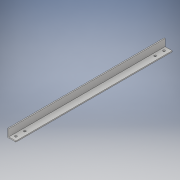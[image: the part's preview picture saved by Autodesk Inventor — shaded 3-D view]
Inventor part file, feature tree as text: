
AUTODESK INVENTOR PART (.ipt)
format: ipt  version: 2017 (Build 210142000, 142)  size: 126,976 bytes
history: native  units: in
note: dims shown in document units (in); Inventor stores cm internally (conversion verified against a paired STEP export)
features: hole x3, sketch x3, extrude x1
ambient origin geometry x8: Origin, YZ Plane, XZ Plane, XY Plane, X Axis, Y Axis, Z Axis, Center Point
bodies: Solid1 (feature_tree)
feature tree (7):
  extrude  "Extrusion1"  Depth=1.0in
  hole  "Hole1"  [1 undecoded]
  hole  "Hole5"  [1 undecoded]
  hole  "Hole6"  [1 undecoded]
  sketch  "Sketch2"  dims[d0=1.0in d1=1.0in]
  sketch  "Sketch8"  dims[d2=0.125in d3=19.375in d4=0.0in]
  sketch  "Sketch9"  dims[d5=0.5in d6=0.5in d7=0.7874in d9=18.375in d10=0.3937in d12=1.0in d14=0.266in d15=0.75in d16=0.385in d17=0.25in d18=0.5635in d19=1.0in d20=0.8108in d31=0.5in d59=0.5in d60=1.6in d61=0.266in d62=0.75in d63=0.507in d64=0.25in d65=0.5635in d66=1.0in d67=0.8108in d68=0.5in d69=1.6in d70=0.266in d71=0.75in d72=0.507in d73=0.25in d74=0.5635in d75=1.0in d76=0.8108in]
note: 3 required parameter values undecoded (feature->parameter linkage not recoverable at this tier; creation-order binding heuristic only, values carry confidence <= 0.55)
